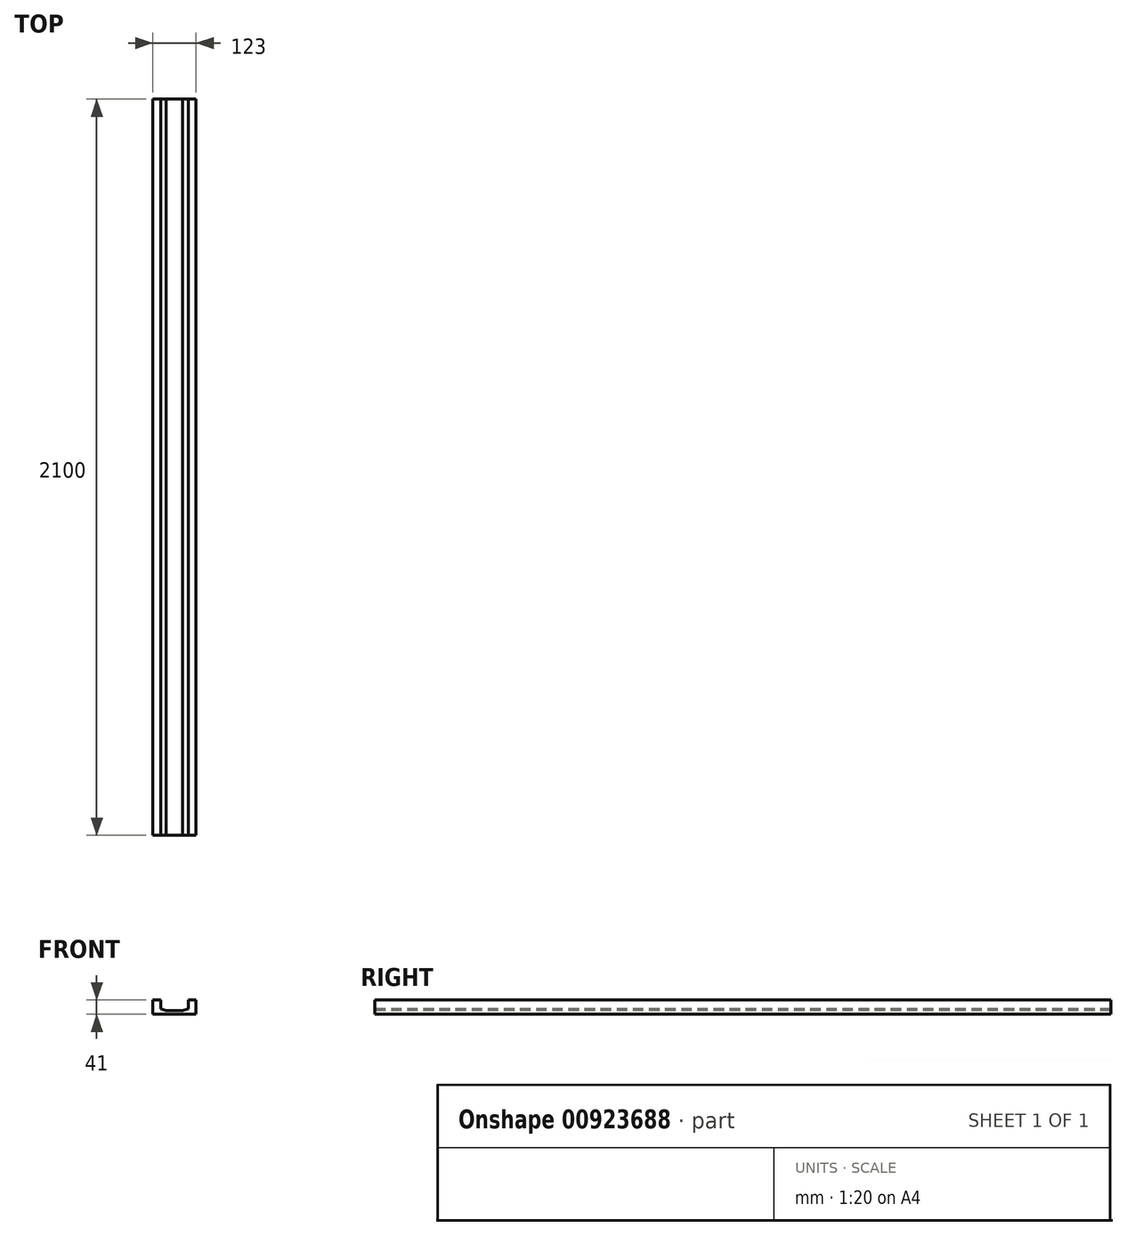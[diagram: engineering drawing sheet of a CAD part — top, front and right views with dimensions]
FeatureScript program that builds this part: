
annotation { "Feature Type Name" : "Feature", "Feature Type Description" : "" }
export const myFeature = defineFeature(function(context is Context, id is Id, definition is map)
    precondition{}
    {
        {
            var Q0;
            Q0=qCreatedBy(makeId("Front.planeOp"),FACE);
            var sketch = newSketch(context, id + "F0", { "sketchPlane" : qUnion([Q0])});
            skLineSegment(sketch, "E0.bottom", {"start": v(-61.5, 20.5) * mm, "end": v(-39.5, 20.5) * mm});
            skLineSegment(sketch, "E0.left", {"start": v(-61.5, 20.5) * mm, "end": v(-61.5, -20.5) * mm});
            skPoint(sketch, "E0.middle", {"position": v(0, 0) * mm});
            skLineSegment(sketch, "E1", {"start": v(-39.5, 20.5) * mm, "end": v(-39.5, -4.5) * mm});
            skLineSegment(sketch, "E2", {"start": v(-39.5, -4.5) * mm, "end": v(-23.5, -9.5) * mm});
            skLineSegment(sketch, "E3", {"start": v(-23.5, -9.5) * mm, "end": v(0, -9.5) * mm});
            skPoint(sketch, "E0.right.start.orphan", {"position": v(61.5, 20.5) * mm});
            skPoint(sketch, "E0.top.end.orphan", {"position": v(61.5, -20.5) * mm});
            skLineSegment(sketch, "E4", {"start": v(-61.5, -20.5) * mm, "end": v(0, -20.5) * mm});
            skLineSegment(sketch, "E5.MirrorCS", {"start": v(61.5, 20.5) * mm, "end": v(39.5, 20.5) * mm});
            skLineSegment(sketch, "E6.MirrorCS", {"start": v(61.5, 20.5) * mm, "end": v(61.5, -20.5) * mm});
            skLineSegment(sketch, "E7.MirrorCS", {"start": v(39.5, 20.5) * mm, "end": v(39.5, -4.5) * mm});
            skLineSegment(sketch, "E8.MirrorCS", {"start": v(39.5, -4.5) * mm, "end": v(23.5, -9.5) * mm});
            skLineSegment(sketch, "E9.MirrorCS", {"start": v(23.5, -9.5) * mm, "end": v(0, -9.5) * mm});
            skLineSegment(sketch, "E10.MirrorCS", {"start": v(61.5, -20.5) * mm, "end": v(0, -20.5) * mm});
            skSolve(sketch);
        }
        {
            var Q0;
            Q0 = qSketchRegion(id + "F0", true);
            extrude(context, id + "F1", {"entities" : qUnion([Q0]), "oppositeDirection" : true, "depth" : 2100 * mm, "offsetDistance" : 25 * mm});
        }
    });
